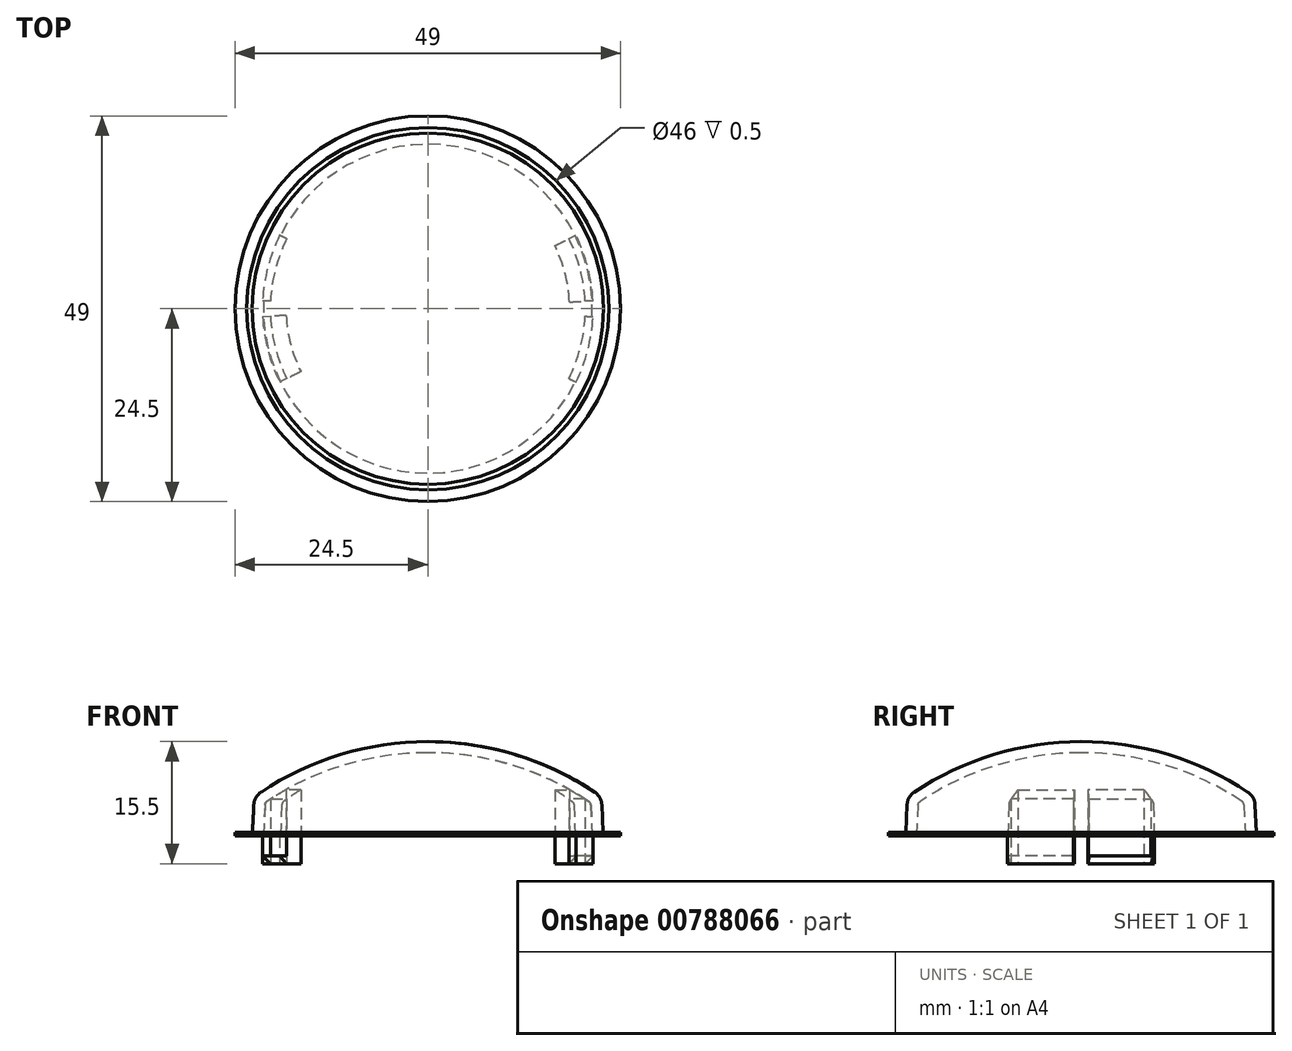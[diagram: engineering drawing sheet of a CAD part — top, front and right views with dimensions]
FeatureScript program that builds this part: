
annotation { "Feature Type Name" : "Feature", "Feature Type Description" : "" }
export const myFeature = defineFeature(function(context is Context, id is Id, definition is map)
    precondition{}
    {
        {
            var Q0;
            Q0=qCreatedBy(makeId("Front.planeOp"),FACE);
            var sketch = newSketch(context, id + "F0", { "sketchPlane" : qUnion([Q0])});
            skLineSegment(sketch, "E0", {"start": v(-4.92, 12) * mm, "end": v(0, 12) * mm, "construction": true});
            skArc(sketch, "E1", {"start": v(0, 12) * mm, "mid": v(11.57, 10.2) * mm, "end": v(22.05, 5) * mm});
            skLineSegment(sketch, "E2", {"start": v(22.05, 5) * mm, "end": v(22.3, 0) * mm});
            skLineSegment(sketch, "E3", {"start": v(0, 12) * mm, "end": v(0, 0) * mm});
            skLineSegment(sketch, "E4", {"start": v(0, 0) * mm, "end": v(22.3, 0) * mm});
            skLineSegment(sketch, "E5.bottom", {"start": v(23, 0) * mm, "end": v(24.5, 0) * mm});
            skLineSegment(sketch, "E5.top", {"start": v(23, 0.5) * mm, "end": v(24.5, 0.5) * mm});
            skLineSegment(sketch, "E5.left", {"start": v(23, 0) * mm, "end": v(23, 0.5) * mm});
            skLineSegment(sketch, "E5.right", {"start": v(24.5, 0) * mm, "end": v(24.5, 0.5) * mm});
            skSolve(sketch);
        }
        {
            var Q0;
            Q0 = qSketchRegion(id + "F0", true);
            var Q1;
            Q1=makeQuery(id+"F0.imprint","IMPRINT",FACE,{"disambiguationData":[TD([[makeQuery(id+"F0.imprint","IMPRINT",EDGE,{"derivedFrom":sQuery(id+"F0.wireOp",EDGE,"E1")}),-1.0]])]});
            var Q2;
            Q2=sQuery(id+"F0.wireOp",EDGE,"E3");
            revolve(context, id + "F1", {"surfaceOperationType" : NewSurfaceOperationType.NEW, "entities" : qUnion([Q0, Q1]), "axis" : qUnion([Q2]), "revolveType" : RevolveType.FULL});
        }
        {
            var Q0;
            Q0=makeQuery(id+"F1.opRevolve","SWEPT_EDGE",EDGE,{"disambiguationData":[OSD([sQuery(id+"F0.wireOp",EDGE,"E1"),sQuery(id+"F0.wireOp",EDGE,"E2")])]});
            fillet(context, id + "F2", {"entities" : qUnion([Q0]), "radius" : 2 * mm, "tangentPropagation" : true, "allowEdgeOverflow" : false});
        }
        {
            var Q0;
            Q0=makeQuery(id+"F1.opRevolve","SWEPT_FACE",FACE,{"disambiguationData":[OSD([sQuery(id+"F0.wireOp",EDGE,"E4")])]});
            shell(context, id + "F3", {"entities" : qUnion([Q0]), "thickness" : 1.4 * mm});
        }
        {
            var Q0;
            Q0=qCreatedBy(makeId("Top.planeOp"),FACE);
            cPlane(context, id + "F4", {"entities" : qUnion([Q0]), "cplaneType" : CPlaneType.OFFSET, "offset" : 3.5 * mm, "oppositeDirection" : true, "width" : 150 * mm, "height" : 150 * mm});
        }
        {
            var Q0;
            Q0=qCreatedBy(id+"F4.planeOp",FACE);
            var sketch = newSketch(context, id + "F5", { "sketchPlane" : qUnion([Q0])});
            skArc(sketch, "E6", {"start": v(20.98, -1) * mm, "mid": v(20.33, -5.27) * mm, "end": v(18.82, -9.32) * mm});
            skLineSegment(sketch, "E7", {"start": v(0, 0) * mm, "end": v(20.98, -1) * mm, "construction": true});
            skLineSegment(sketch, "E8", {"start": v(18.82, -9.32) * mm, "end": v(0, 0) * mm, "construction": true});
            skArc(sketch, "E9", {"start": v(19.98, -0.95) * mm, "mid": v(19.36, -5.02) * mm, "end": v(17.92, -8.88) * mm});
            skArc(sketch, "E10", {"start": v(17.98, -0.86) * mm, "mid": v(17.42, -4.52) * mm, "end": v(16.13, -8) * mm});
            skLineSegment(sketch, "E11", {"start": v(17.98, -0.86) * mm, "end": v(20.98, -1) * mm});
            skLineSegment(sketch, "E12", {"start": v(16.13, -8) * mm, "end": v(18.82, -9.32) * mm});
            skLineSegment(sketch, "E13.MirrorCS", {"start": v(17.98, 0.86) * mm, "end": v(20.98, 1) * mm});
            skLineSegment(sketch, "E14.MirrorCS", {"start": v(16.13, 8) * mm, "end": v(18.82, 9.32) * mm});
            skArc(sketch, "E15.MirrorCS", {"start": v(17.98, 0.86) * mm, "mid": v(17.42, 4.52) * mm, "end": v(16.13, 8) * mm});
            skArc(sketch, "E16.MirrorCS", {"start": v(20.98, 1) * mm, "mid": v(20.33, 5.27) * mm, "end": v(18.82, 9.32) * mm});
            skArc(sketch, "E17.MirrorCS", {"start": v(19.98, 0.95) * mm, "mid": v(19.36, 5.02) * mm, "end": v(17.92, 8.88) * mm});
            skLineSegment(sketch, "E18.MirrorCS", {"start": v(-17.98, -0.86) * mm, "end": v(-20.98, -1) * mm});
            skLineSegment(sketch, "E19.MirrorCS", {"start": v(-17.98, 0.86) * mm, "end": v(-20.98, 1) * mm});
            skLineSegment(sketch, "E20.MirrorCS", {"start": v(-16.13, 8) * mm, "end": v(-18.82, 9.32) * mm});
            skLineSegment(sketch, "E21.MirrorCS", {"start": v(-16.13, -8) * mm, "end": v(-18.82, -9.32) * mm});
            skArc(sketch, "E22.MirrorCS", {"start": v(-20.98, 1) * mm, "mid": v(-20.33, 5.27) * mm, "end": v(-18.82, 9.32) * mm});
            skArc(sketch, "E23.MirrorCS", {"start": v(-20.98, -1) * mm, "mid": v(-20.33, -5.27) * mm, "end": v(-18.82, -9.32) * mm});
            skArc(sketch, "E24.MirrorCS", {"start": v(-19.98, -0.95) * mm, "mid": v(-19.36, -5.02) * mm, "end": v(-17.92, -8.88) * mm});
            skArc(sketch, "E25.MirrorCS", {"start": v(-19.98, 0.95) * mm, "mid": v(-19.36, 5.02) * mm, "end": v(-17.92, 8.88) * mm});
            skArc(sketch, "E26.MirrorCS", {"start": v(-17.98, -0.86) * mm, "mid": v(-17.42, -4.52) * mm, "end": v(-16.13, -8) * mm});
            skArc(sketch, "E27.MirrorCS", {"start": v(-17.98, 0.86) * mm, "mid": v(-17.42, 4.52) * mm, "end": v(-16.13, 8) * mm});
            skSolve(sketch);
        }
        {
            var Q0;
            {var subQ0=sQuery(id+"F5.wireOp",EDGE,"E15.MirrorCS");Q0=makeQuery(id+"F5.imprint","IMPRINT",FACE,{"disambiguationData":[TD([[makeQuery(id+"F5.imprint","IMPRINT",EDGE,{"derivedFrom":subQ0}),-1.0]])]});}
            var Q1;
            {var subQ0=sQuery(id+"F5.wireOp",EDGE,"E9");Q1=makeQuery(id+"F5.imprint","IMPRINT",FACE,{"disambiguationData":[TD([[makeQuery(id+"F5.imprint","IMPRINT",EDGE,{"derivedFrom":subQ0}),-1.0]])]});}
            var Q2;
            {var subQ2=sQuery(id+"F5.wireOp",EDGE,"E24.MirrorCS");Q2=makeQuery(id+"F5.imprint","IMPRINT",FACE,{"disambiguationData":[TD([[makeQuery(id+"F5.imprint","IMPRINT",EDGE,{"derivedFrom":subQ2}),1.0]])]});}
            var Q3;
            {var subQ2=sQuery(id+"F5.wireOp",EDGE,"E25.MirrorCS");Q3=makeQuery(id+"F5.imprint","IMPRINT",FACE,{"disambiguationData":[TD([[makeQuery(id+"F5.imprint","IMPRINT",EDGE,{"derivedFrom":subQ2}),-1.0]])]});}
            extrude(context, id + "F6", {"entities" : qUnion([Q0, Q1, Q2, Q3]), "operationType" : NewBodyOperationType.ADD, "endBound" : BoundingType.UP_TO_NEXT, "depth" : 25 * mm, "offsetDistance" : 25 * mm});
        }
        {
            var Q0;
            {var subQ0=sQuery(id+"F5.wireOp",EDGE,"E23.MirrorCS");Q0=makeQuery(id+"F5.imprint","IMPRINT",FACE,{"disambiguationData":[TD([[makeQuery(id+"F5.imprint","IMPRINT",EDGE,{"derivedFrom":subQ0}),1.0]])]});}
            var Q1;
            {var subQ0=sQuery(id+"F5.wireOp",EDGE,"E22.MirrorCS");Q1=makeQuery(id+"F5.imprint","IMPRINT",FACE,{"disambiguationData":[TD([[makeQuery(id+"F5.imprint","IMPRINT",EDGE,{"derivedFrom":subQ0}),-1.0]])]});}
            var Q2;
            {var subQ0=sQuery(id+"F5.wireOp",EDGE,"E16.MirrorCS");Q2=makeQuery(id+"F5.imprint","IMPRINT",FACE,{"disambiguationData":[TD([[makeQuery(id+"F5.imprint","IMPRINT",EDGE,{"derivedFrom":subQ0}),1.0]])]});}
            var Q3;
            {var subQ0=sQuery(id+"F5.wireOp",EDGE,"E6");Q3=makeQuery(id+"F5.imprint","IMPRINT",FACE,{"disambiguationData":[TD([[makeQuery(id+"F5.imprint","IMPRINT",EDGE,{"derivedFrom":subQ0}),-1.0]])]});}
            extrude(context, id + "F7", {"entities" : qUnion([Q0, Q1, Q2, Q3]), "operationType" : NewBodyOperationType.ADD, "depth" : 1 * mm, "offsetDistance" : 25 * mm});
        }
        {
            var Q0;
            Q0=makeQuery(id+"F7.opExtrude","CAP_EDGE",EDGE,{"disambiguationData":[OSD([sQuery(id+"F5.wireOp",EDGE,"E23.MirrorCS")])],"isStart":true});
            var Q1;
            Q1=makeQuery(id+"F7.opExtrude","CAP_EDGE",EDGE,{"disambiguationData":[OSD([sQuery(id+"F5.wireOp",EDGE,"E22.MirrorCS")])],"isStart":true});
            var Q2;
            Q2=makeQuery(id+"F7.opExtrude","CAP_EDGE",EDGE,{"disambiguationData":[OSD([sQuery(id+"F5.wireOp",EDGE,"E6")])],"isStart":true});
            var Q3;
            Q3=makeQuery(id+"F7.opExtrude","CAP_EDGE",EDGE,{"disambiguationData":[OSD([sQuery(id+"F5.wireOp",EDGE,"E16.MirrorCS")])],"isStart":true});
            var Q4;
            Q4=makeQuery(id+"F6.opExtrude","CAP_EDGE",EDGE,{"disambiguationData":[OSD([sQuery(id+"F5.wireOp",EDGE,"E26.MirrorCS")])],"isStart":false});
            var Q5;
            Q5=makeQuery(id+"F6.opExtrude","CAP_EDGE",EDGE,{"disambiguationData":[OSD([sQuery(id+"F5.wireOp",EDGE,"E27.MirrorCS")])],"isStart":false});
            var Q6;
            Q6=makeQuery(id+"F6.opExtrude","CAP_EDGE",EDGE,{"disambiguationData":[OSD([sQuery(id+"F5.wireOp",EDGE,"E15.MirrorCS")])],"isStart":false});
            var Q7;
            Q7=makeQuery(id+"F6.opExtrude","CAP_EDGE",EDGE,{"disambiguationData":[OSD([sQuery(id+"F5.wireOp",EDGE,"E10")])],"isStart":false});
            chamfer(context, id + "F8", {"entities" : qUnion([Q0, Q1, Q2, Q3, Q4, Q5, Q6, Q7]), "width" : 1 * mm, "tangentPropagation" : true});
        }
    });
